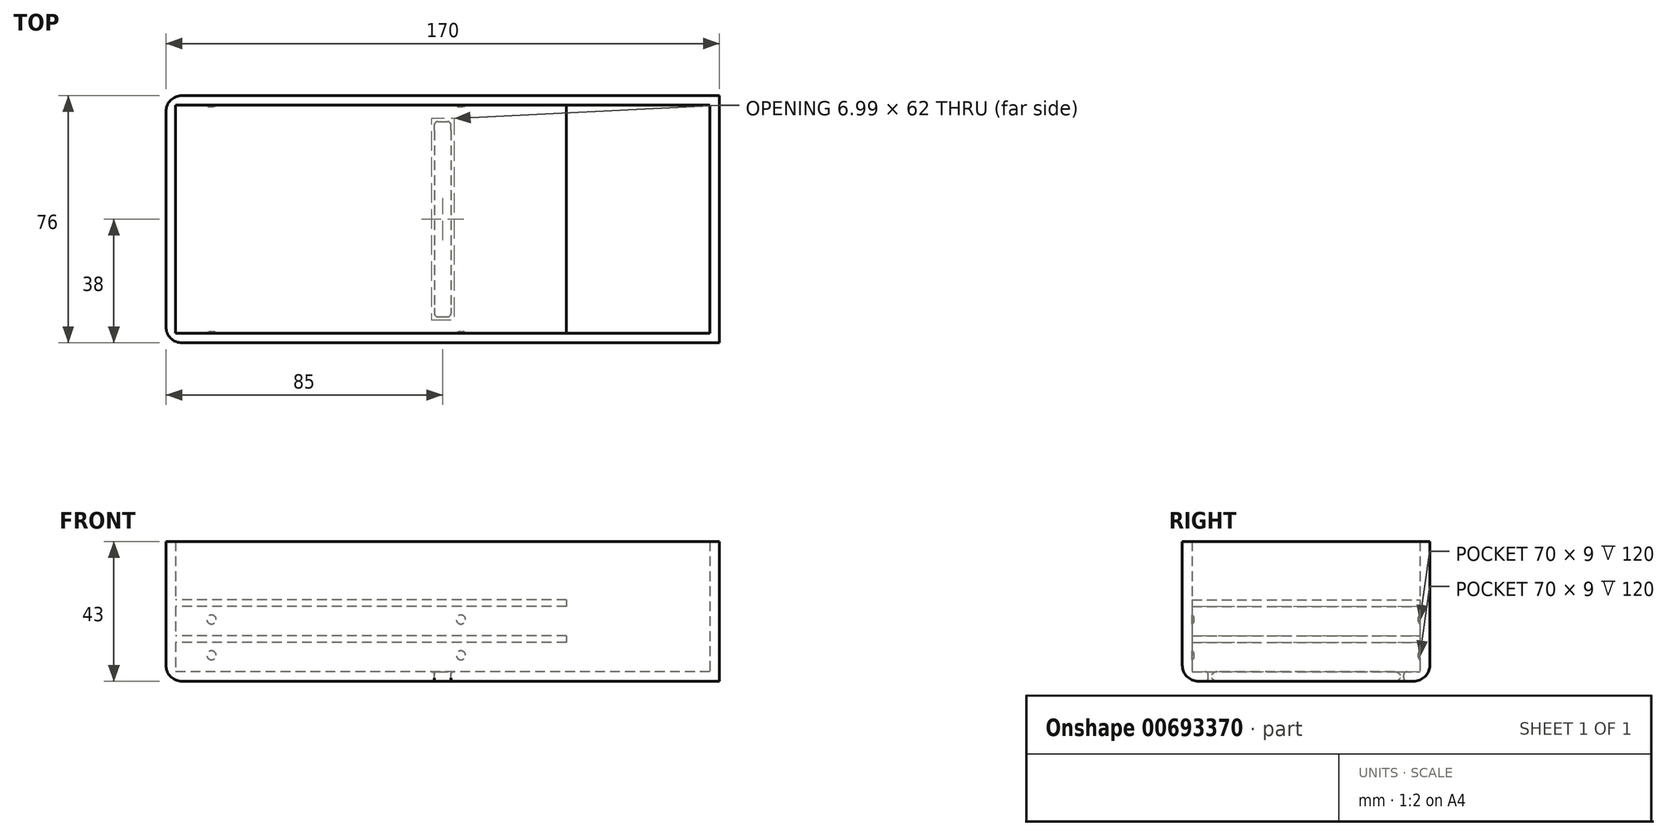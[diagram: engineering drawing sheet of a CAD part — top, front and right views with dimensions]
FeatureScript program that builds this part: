
annotation { "Feature Type Name" : "Feature", "Feature Type Description" : "" }
export const myFeature = defineFeature(function(context is Context, id is Id, definition is map)
    precondition{}
    {
        {
            var Q0;
            Q0=qCreatedBy(makeId("Top.planeOp"),FACE);
            var sketch = newSketch(context, id + "F0", { "sketchPlane" : qUnion([Q0])});
            skLineSegment(sketch, "E0.bottom", {"start": v(85, -38) * mm, "end": v(-85, -38) * mm});
            skLineSegment(sketch, "E0.top", {"start": v(85, 38) * mm, "end": v(-85, 38) * mm});
            skLineSegment(sketch, "E0.left", {"start": v(85, -38) * mm, "end": v(85, 38) * mm});
            skLineSegment(sketch, "E0.right", {"start": v(-85, -38) * mm, "end": v(-85, 38) * mm});
            skPoint(sketch, "E0.middle", {"position": v(0, 0) * mm});
            skLineSegment(sketch, "E1.bottom", {"start": v(82, -35) * mm, "end": v(-82, -35) * mm});
            skLineSegment(sketch, "E1.top", {"start": v(82, 35) * mm, "end": v(-82, 35) * mm});
            skLineSegment(sketch, "E1.left", {"start": v(82, -35) * mm, "end": v(82, 35) * mm});
            skLineSegment(sketch, "E1.right", {"start": v(-82, -35) * mm, "end": v(-82, 35) * mm});
            skSolve(sketch);
        }
        {
            var Q0;
            Q0=makeQuery(id+"F0.imprint","IMPRINT",FACE,{"disambiguationData":[TD([[makeQuery(id+"F0.imprint","IMPRINT",EDGE,{"derivedFrom":sQuery(id+"F0.wireOp",EDGE,"E1.bottom")}),-1.0]])]});
            var Q1;
            Q1=makeQuery(id+"F0.imprint","IMPRINT",FACE,{"disambiguationData":[TD([[makeQuery(id+"F0.imprint","IMPRINT",EDGE,{"derivedFrom":sQuery(id+"F0.wireOp",EDGE,"E0.bottom")}),-1.0]])]});
            extrude(context, id + "F1", {"entities" : qUnion([Q0, Q1]), "oppositeDirection" : true, "depth" : 3 * mm, "offsetDistance" : 25 * mm});
        }
        {
            var Q0;
            Q0=makeQuery(id+"F0.imprint","IMPRINT",FACE,{"disambiguationData":[TD([[makeQuery(id+"F0.imprint","IMPRINT",EDGE,{"derivedFrom":sQuery(id+"F0.wireOp",EDGE,"E0.bottom")}),-1.0]])]});
            extrude(context, id + "F2", {"entities" : qUnion([Q0]), "operationType" : NewBodyOperationType.ADD, "depth" : 40 * mm, "offsetDistance" : 25 * mm});
        }
        {
            var Q0;
            Q0=qCreatedBy(makeId("Front.planeOp"),FACE);
            var sketch = newSketch(context, id + "F3", { "sketchPlane" : qUnion([Q0])});
            skLineSegment(sketch, "E2", {"start": v(0, 0) * mm, "end": v(0, 9) * mm});
            skLineSegment(sketch, "E3.0", {"start": v(90, -8) * mm, "end": v(90, 45) * mm});
            skLineSegment(sketch, "E3.1", {"start": v(-90, -8) * mm, "end": v(90, -8) * mm});
            skLineSegment(sketch, "E3.2", {"start": v(-90, 45) * mm, "end": v(-90, -8) * mm});
            skLineSegment(sketch, "E3.3", {"start": v(90, 45) * mm, "end": v(-90, 45) * mm});
            skLineSegment(sketch, "E4", {"start": v(-82, 9) * mm, "end": v(38, 9) * mm});
            skLineSegment(sketch, "E5.0", {"start": v(-82, 11) * mm, "end": v(38, 11) * mm});
            skLineSegment(sketch, "E6.0", {"start": v(-82, 20) * mm, "end": v(38, 20) * mm});
            skLineSegment(sketch, "E7.0", {"start": v(-82, 22) * mm, "end": v(38, 22) * mm});
            skLineSegment(sketch, "E8", {"start": v(38, 9) * mm, "end": v(38, 11) * mm});
            skLineSegment(sketch, "E9", {"start": v(38, 20) * mm, "end": v(38, 22) * mm});
            skLineSegment(sketch, "E10", {"start": v(-82, 9) * mm, "end": v(-82, 11) * mm});
            skLineSegment(sketch, "E11", {"start": v(-82, 20) * mm, "end": v(-82, 22) * mm});
            skLineSegment(sketch, "E12", {"start": v(-71, 9) * mm, "end": v(-71, 5) * mm});
            skLineSegment(sketch, "E13", {"start": v(-71, 20) * mm, "end": v(-71, 16) * mm});
            skLineSegment(sketch, "E14", {"start": v(5.6, 20) * mm, "end": v(5.6, 16) * mm});
            skLineSegment(sketch, "E15", {"start": v(5.6, 9) * mm, "end": v(5.6, 5) * mm});
            skSolve(sketch);
        }
        {
            var Q0;
            Q0=makeQuery(id+"F3.imprint","IMPRINT",FACE,{"disambiguationData":[TD([[makeQuery(id+"F3.imprint","IMPRINT",EDGE,{"derivedFrom":sQuery(id+"F3.wireOp",EDGE,"E5.0")}),-1.0]])]});
            extrude(context, id + "F4", {"entities" : qUnion([Q0]), "operationType" : NewBodyOperationType.ADD, "endBound" : BoundingType.SYMMETRIC, "depth" : 71.8 * mm, "offsetDistance" : 25 * mm});
        }
        {
            var Q0;
            Q0=makeQuery(id+"F3.imprint","IMPRINT",FACE,{"disambiguationData":[TD([[makeQuery(id+"F3.imprint","IMPRINT",EDGE,{"derivedFrom":sQuery(id+"F3.wireOp",EDGE,"E6.0")}),1.0]])]});
            extrude(context, id + "F5", {"entities" : qUnion([Q0]), "operationType" : NewBodyOperationType.ADD, "endBound" : BoundingType.SYMMETRIC, "depth" : 72.8 * mm, "offsetDistance" : 25 * mm});
        }
        {
            var Q0;
            Q0=makeQuery(id+"F2.opExtrude","SWEPT_FACE",FACE,{"disambiguationData":[OSD([sQuery(id+"F0.wireOp",EDGE,"E1.top")])]});
            var sketch = newSketch(context, id + "F6", { "sketchPlane" : qUnion([Q0])});
            skCircle(sketch, "E16", {"center": v(-71, 16) * mm, "radius": 1.4 * mm});
            skCircle(sketch, "E17", {"center": v(-71, 5) * mm, "radius": 1.4 * mm});
            skCircle(sketch, "E18", {"center": v(5.6, 5) * mm, "radius": 1.4 * mm});
            skCircle(sketch, "E19", {"center": v(5.6, 16) * mm, "radius": 1.4 * mm});
            skSolve(sketch);
        }
        {
            var Q0;
            Q0 = qSketchRegion(id + "F6", true);
            extrude(context, id + "F7", {"entities" : qUnion([Q0]), "operationType" : NewBodyOperationType.ADD, "depth" : 0.5 * mm, "offsetDistance" : 25 * mm});
        }
        {
            var Q0;
            Q0=makeQuery(id+"F7.opExtrude","CAP_EDGE",EDGE,{"disambiguationData":[OSD([sQuery(id+"F6.wireOp",EDGE,"E16")])],"isStart":false});
            var Q1;
            Q1=makeQuery(id+"F7.opExtrude","CAP_EDGE",EDGE,{"disambiguationData":[OSD([sQuery(id+"F6.wireOp",EDGE,"E17")])],"isStart":false});
            var Q2;
            Q2=makeQuery(id+"F7.opExtrude","CAP_EDGE",EDGE,{"disambiguationData":[OSD([sQuery(id+"F6.wireOp",EDGE,"E19")])],"isStart":false});
            var Q3;
            Q3=makeQuery(id+"F7.opExtrude","CAP_EDGE",EDGE,{"disambiguationData":[OSD([sQuery(id+"F6.wireOp",EDGE,"E18")])],"isStart":false});
            fillet(context, id + "F8", {"entities" : qUnion([Q0, Q1, Q2, Q3]), "radius" : 1 * mm, "tangentPropagation" : true, "allowEdgeOverflow" : false});
        }
        {
            var Q0;
            Q0=makeQuery(id+"F2.opExtrude","SWEPT_FACE",FACE,{"disambiguationData":[OSD([sQuery(id+"F0.wireOp",EDGE,"E1.bottom")])]});
            var sketch = newSketch(context, id + "F9", { "sketchPlane" : qUnion([Q0])});
            skCircle(sketch, "E20", {"center": v(71, 16) * mm, "radius": 1.4 * mm});
            skCircle(sketch, "E21", {"center": v(-5.6, 16) * mm, "radius": 1.4 * mm});
            skCircle(sketch, "E22", {"center": v(-5.6, 5) * mm, "radius": 1.4 * mm});
            skCircle(sketch, "E23", {"center": v(71, 5) * mm, "radius": 1.4 * mm});
            skSolve(sketch);
        }
        {
            var Q0;
            Q0 = qSketchRegion(id + "F9", true);
            extrude(context, id + "F10", {"entities" : qUnion([Q0]), "operationType" : NewBodyOperationType.ADD, "depth" : 0.5 * mm, "offsetDistance" : 25 * mm});
        }
        {
            var Q0;
            Q0=makeQuery(id+"F10.opExtrude","CAP_EDGE",EDGE,{"disambiguationData":[OSD([sQuery(id+"F9.wireOp",EDGE,"E20")])],"isStart":false});
            var Q1;
            Q1=makeQuery(id+"F10.opExtrude","CAP_EDGE",EDGE,{"disambiguationData":[OSD([sQuery(id+"F9.wireOp",EDGE,"E23")])],"isStart":false});
            var Q2;
            Q2=makeQuery(id+"F10.opExtrude","CAP_EDGE",EDGE,{"disambiguationData":[OSD([sQuery(id+"F9.wireOp",EDGE,"E21")])],"isStart":false});
            var Q3;
            Q3=makeQuery(id+"F10.opExtrude","CAP_EDGE",EDGE,{"disambiguationData":[OSD([sQuery(id+"F9.wireOp",EDGE,"E22")])],"isStart":false});
            fillet(context, id + "F11", {"entities" : qUnion([Q0, Q1, Q2, Q3]), "radius" : 1 * mm, "tangentPropagation" : true, "allowEdgeOverflow" : false});
        }
        {
            var Q0;
            {var subQ0=sQuery(id+"F0.wireOp",EDGE,"E0.right");var subQ1=sQuery(id+"F0.wireOp",EDGE,"E0.top");Q0=makeQuery(id+"F2.boolean.opBoolean","MERGE",EDGE,{"derivedFrom":[makeQuery(id+"F1.opExtrude","SWEPT_EDGE",EDGE,{"disambiguationData":[OSD([subQ1,subQ0])]}),makeQuery(id+"F2.opExtrude","SWEPT_EDGE",EDGE,{"disambiguationData":[OSD([subQ1,subQ0])]})]});}
            var Q1;
            {var subQ0=sQuery(id+"F0.wireOp",EDGE,"E0.right");var subQ1=sQuery(id+"F0.wireOp",EDGE,"E0.bottom");Q1=makeQuery(id+"F2.boolean.opBoolean","MERGE",EDGE,{"derivedFrom":[makeQuery(id+"F1.opExtrude","SWEPT_EDGE",EDGE,{"disambiguationData":[OSD([subQ1,subQ0])]}),makeQuery(id+"F2.opExtrude","SWEPT_EDGE",EDGE,{"disambiguationData":[OSD([subQ1,subQ0])]})]});}
            var Q2;
            Q2=makeQuery(id+"F1.opExtrude","CAP_EDGE",EDGE,{"disambiguationData":[OSD([sQuery(id+"F0.wireOp",EDGE,"E0.right")])],"isStart":false});
            var Q3;
            Q3=makeQuery(id+"F1.opExtrude","CAP_EDGE",EDGE,{"disambiguationData":[OSD([sQuery(id+"F0.wireOp",EDGE,"E0.top")])],"isStart":false});
            var Q4;
            Q4=makeQuery(id+"F1.opExtrude","CAP_EDGE",EDGE,{"disambiguationData":[OSD([sQuery(id+"F0.wireOp",EDGE,"E0.bottom")])],"isStart":false});
            fillet(context, id + "F12", {"entities" : qUnion([Q0, Q1, Q2, Q3, Q4]), "radius" : 5 * mm, "tangentPropagation" : true, "allowEdgeOverflow" : false});
        }
        {
            var Q0;
            Q0=makeQuery(id+"F0.imprint","IMPRINT",FACE,{"disambiguationData":[TD([[makeQuery(id+"F0.imprint","IMPRINT",EDGE,{"derivedFrom":sQuery(id+"F0.wireOp",EDGE,"E1.bottom")}),-1.0]])]});
            var sketch = newSketch(context, id + "F13", { "sketchPlane" : qUnion([Q0])});
            skLineSegment(sketch, "E24.bottom", {"start": v(-2.5, 30) * mm, "end": v(2.5, 30) * mm});
            skLineSegment(sketch, "E24.top", {"start": v(-2.5, -30) * mm, "end": v(2.5, -30) * mm});
            skLineSegment(sketch, "E24.left", {"start": v(-2.5, 30) * mm, "end": v(-2.5, -30) * mm});
            skLineSegment(sketch, "E24.right", {"start": v(2.5, 30) * mm, "end": v(2.5, -30) * mm});
            skPoint(sketch, "E24.middle", {"position": v(0, 0) * mm});
            skSolve(sketch);
        }
        {
            var Q0;
            Q0 = qSketchRegion(id + "F13", true);
            extrude(context, id + "F14", {"entities" : qUnion([Q0]), "operationType" : NewBodyOperationType.REMOVE, "oppositeDirection" : true, "depth" : 5 * mm, "offsetDistance" : 25 * mm});
        }
        {
            var Q0;
            Q0=makeQuery(id+"F14.boolean.opBoolean","COPY",FACE,{"derivedFrom":makeQuery(id+"F14.opExtrude","SWEPT_FACE",FACE,{"disambiguationData":[OSD([sQuery(id+"F13.wireOp",EDGE,"E24.bottom")])]})});
            var Q1;
            Q1=makeQuery(id+"F14.boolean.opBoolean","COPY",FACE,{"derivedFrom":makeQuery(id+"F14.opExtrude","SWEPT_FACE",FACE,{"disambiguationData":[OSD([sQuery(id+"F13.wireOp",EDGE,"E24.top")])]})});
            fillet(context, id + "F15", {"entities" : qUnion([Q0, Q1]), "radius" : 1 * mm, "tangentPropagation" : true, "allowEdgeOverflow" : false});
        }
    });
